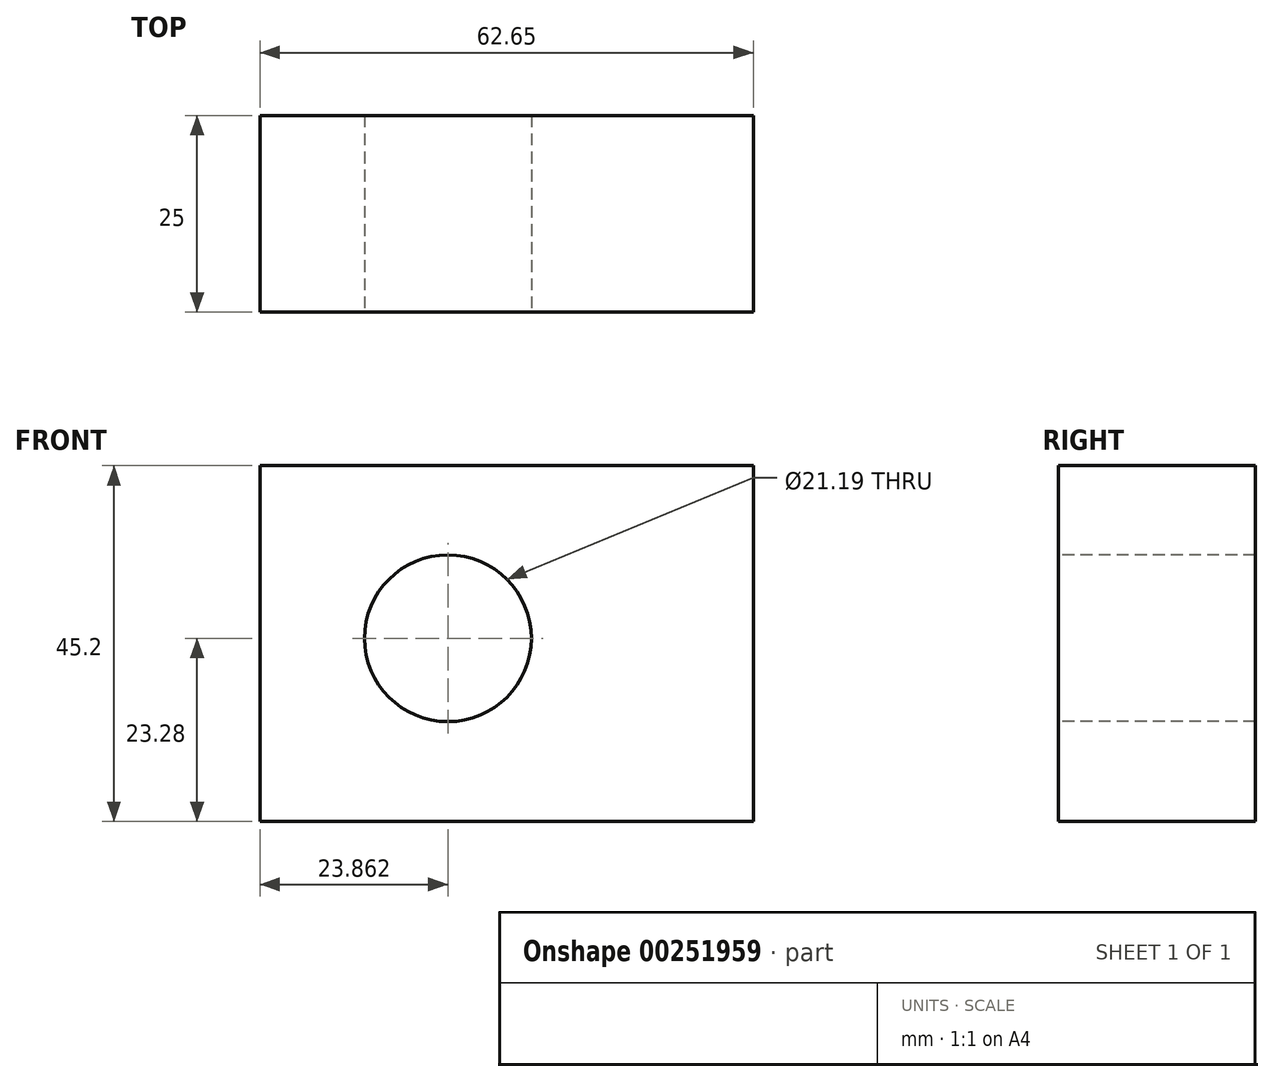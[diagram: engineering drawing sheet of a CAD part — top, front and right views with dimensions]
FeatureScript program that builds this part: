
annotation { "Feature Type Name" : "Feature", "Feature Type Description" : "" }
export const myFeature = defineFeature(function(context is Context, id is Id, definition is map)
    precondition{}
    {
        {
            var Q0;
            Q0=qCreatedBy(makeId("Front.planeOp"),FACE);
            var sketch = newSketch(context, id + "F0", { "sketchPlane" : qUnion([Q0])});
            skLineSegment(sketch, "E0.bottom", {"start": v(-22.3, 21.92) * mm, "end": v(40.34, 21.92) * mm});
            skLineSegment(sketch, "E0.top", {"start": v(-22.3, -23.28) * mm, "end": v(40.34, -23.28) * mm});
            skLineSegment(sketch, "E0.left", {"start": v(-22.3, 21.92) * mm, "end": v(-22.3, -23.28) * mm});
            skLineSegment(sketch, "E0.right", {"start": v(40.34, 21.92) * mm, "end": v(40.34, -23.28) * mm});
            skSolve(sketch);
        }
        {
            var Q0;
            Q0 = qSketchRegion(id + "F0", true);
            extrude(context, id + "F1", {"entities" : qUnion([Q0]), "depth" : 25 * mm});
        }
        {
            var Q0;
            Q0=makeQuery(id+"F1.opExtrude","CAP_FACE",FACE,{"disambiguationData":[OSD([sQuery(id+"F0.wireOp",EDGE,"E0.bottom"),sQuery(id+"F0.wireOp",EDGE,"E0.top"),sQuery(id+"F0.wireOp",EDGE,"E0.left"),sQuery(id+"F0.wireOp",EDGE,"E0.right")])],"isStart":false});
            var sketch = newSketch(context, id + "F2", { "sketchPlane" : qUnion([Q0])});
            skCircle(sketch, "E1", {"center": v(1.55, 0) * mm, "radius": 10.6 * mm});
            skSolve(sketch);
        }
        {
            var Q0;
            Q0=makeQuery(id+"F2.imprint","IMPRINT",FACE,{"disambiguationData":[TD([[makeQuery(id+"F2.imprint","IMPRINT",EDGE,{"derivedFrom":sQuery(id+"F2.wireOp",EDGE,"E1")}),1.0]])]});
            extrude(context, id + "F3", {"entities" : qUnion([Q0]), "operationType" : NewBodyOperationType.REMOVE, "oppositeDirection" : true, "depth" : 25 * mm});
        }
        {
            var Q0;
            Q0=makeQuery(id+"F1.opExtrude","CAP_FACE",FACE,{"disambiguationData":[OSD([sQuery(id+"F0.wireOp",EDGE,"E0.bottom"),sQuery(id+"F0.wireOp",EDGE,"E0.top"),sQuery(id+"F0.wireOp",EDGE,"E0.left"),sQuery(id+"F0.wireOp",EDGE,"E0.right")])],"isStart":false});
            var sketch = newSketch(context, id + "F4", { "sketchPlane" : qUnion([Q0])});
            skCircle(sketch, "E2", {"center": v(26.77, 0) * mm, "radius": 6.56 * mm});
            skSolve(sketch);
        }
        {
            var Q0;
            Q0=makeQuery(id+"F4.imprint","IMPRINT",FACE,{"disambiguationData":[TD([[makeQuery(id+"F4.imprint","IMPRINT",EDGE,{"derivedFrom":sQuery(id+"F4.wireOp",EDGE,"E2")}),1.0]])]});
            extrude(context, id + "F5", {"entities" : qUnion([Q0]), "operationType" : NewBodyOperationType.ADD, "oppositeDirection" : true, "depth" : 25 * mm});
        }
    });
